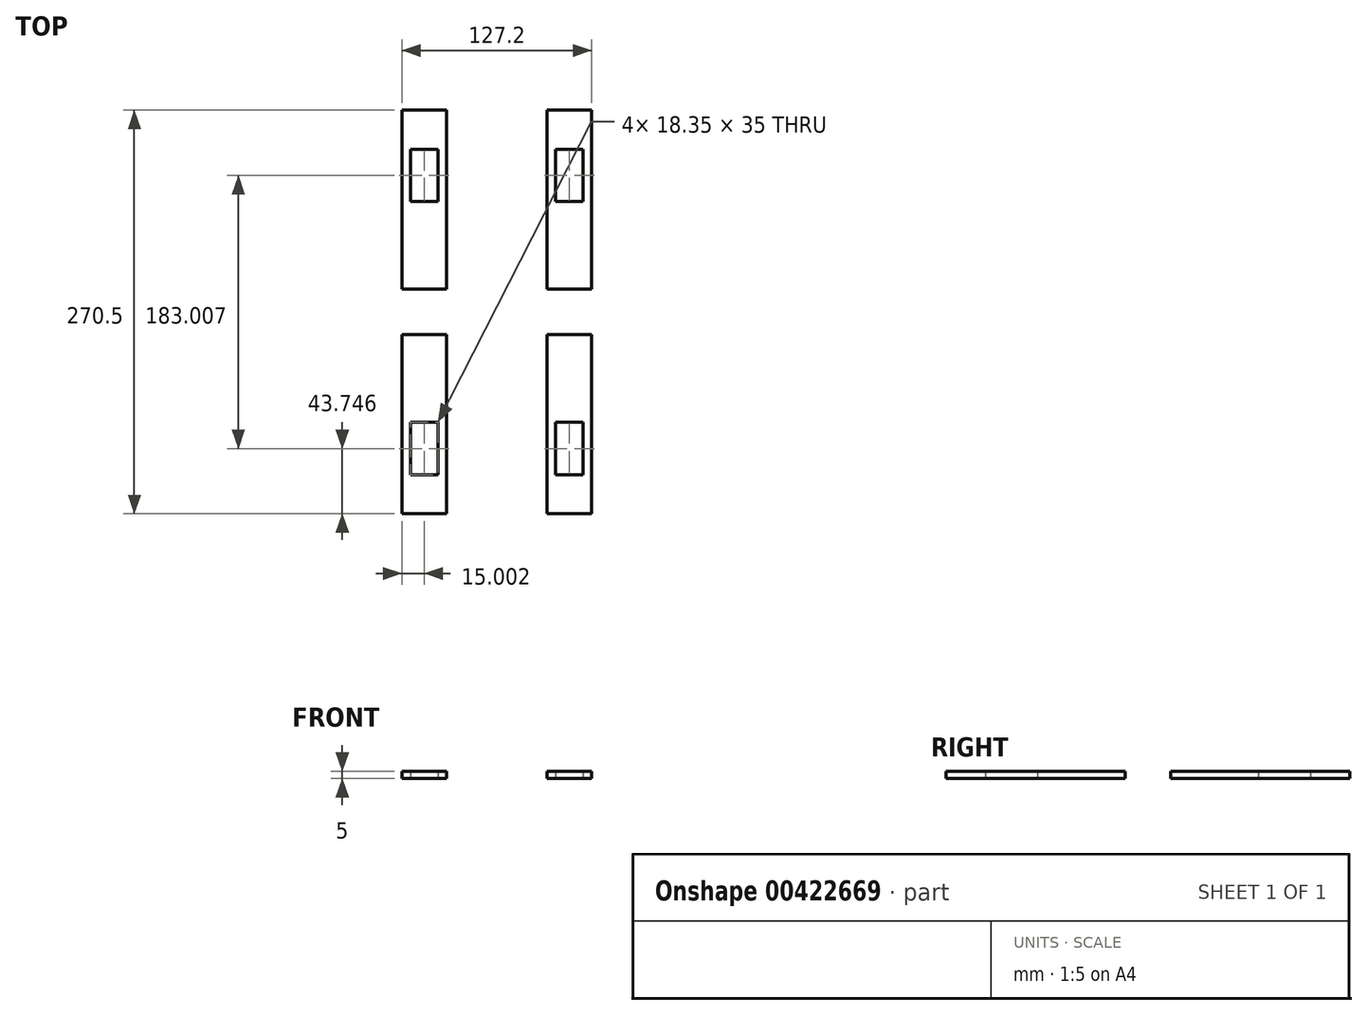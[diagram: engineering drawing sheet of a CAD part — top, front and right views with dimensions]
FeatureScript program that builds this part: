
annotation { "Feature Type Name" : "Feature", "Feature Type Description" : "" }
export const myFeature = defineFeature(function(context is Context, id is Id, definition is map)
    precondition{}
    {
        {
            var Q0;
            Q0=qCreatedBy(makeId("Top.planeOp"),FACE);
            var sketch = newSketch(context, id + "F0", { "sketchPlane" : qUnion([Q0])});
            skLineSegment(sketch, "E0", {"start": v(-63.6, 15.25) * mm, "end": v(-63.6, 135.25) * mm});
            skLineSegment(sketch, "E1", {"start": v(-63.6, 135.25) * mm, "end": v(-33.6, 135.25) * mm});
            skLineSegment(sketch, "E2", {"start": v(-63.6, 15.25) * mm, "end": v(-33.6, 15.25) * mm});
            skLineSegment(sketch, "E3", {"start": v(-33.6, 15.25) * mm, "end": v(-33.6, 135.25) * mm});
            skLineSegment(sketch, "E4.bottom", {"start": v(-39.42, 74) * mm, "end": v(-57.77, 74) * mm});
            skLineSegment(sketch, "E4.top", {"start": v(-39.42, 109) * mm, "end": v(-57.77, 109) * mm});
            skLineSegment(sketch, "E4.left", {"start": v(-39.42, 74) * mm, "end": v(-39.42, 109) * mm});
            skLineSegment(sketch, "E4.right", {"start": v(-57.77, 74) * mm, "end": v(-57.77, 109) * mm});
            skPoint(sketch, "E4.middle", {"position": v(-48.6, 91.5) * mm});
            skLineSegment(sketch, "E5.MirrorCS", {"start": v(-57.77, 74) * mm, "end": v(-39.42, 74) * mm});
            skLineSegment(sketch, "E6.MirrorCS", {"start": v(-57.77, 109) * mm, "end": v(-39.42, 109) * mm});
            skLineSegment(sketch, "E7.MirrorCS", {"start": v(-33.6, 135.25) * mm, "end": v(-63.6, 135.25) * mm});
            skLineSegment(sketch, "E8.MirrorCS", {"start": v(-33.6, 15.25) * mm, "end": v(-63.6, 15.25) * mm});
            skLineSegment(sketch, "E9.MirrorCS", {"start": v(57.77, 74) * mm, "end": v(57.77, 109) * mm});
            skLineSegment(sketch, "E10.MirrorCS", {"start": v(57.77, 74) * mm, "end": v(39.42, 74) * mm});
            skPoint(sketch, "E11.MirrorP", {"position": v(48.6, 91.5) * mm});
            skLineSegment(sketch, "E12.MirrorCS", {"start": v(33.6, 15.25) * mm, "end": v(63.6, 15.25) * mm});
            skLineSegment(sketch, "E13.MirrorCS", {"start": v(39.42, 74) * mm, "end": v(39.42, 109) * mm});
            skLineSegment(sketch, "E14.MirrorCS", {"start": v(57.77, 109) * mm, "end": v(39.42, 109) * mm});
            skLineSegment(sketch, "E15.MirrorCS", {"start": v(39.42, 74) * mm, "end": v(57.77, 74) * mm});
            skLineSegment(sketch, "E16.MirrorCS", {"start": v(63.6, 135.25) * mm, "end": v(33.6, 135.25) * mm});
            skLineSegment(sketch, "E17.MirrorCS", {"start": v(63.6, 15.25) * mm, "end": v(63.6, 135.25) * mm});
            skLineSegment(sketch, "E18.MirrorCS", {"start": v(33.6, 15.25) * mm, "end": v(33.6, 135.25) * mm});
            skLineSegment(sketch, "E19.MirrorCS", {"start": v(33.6, 135.25) * mm, "end": v(63.6, 135.25) * mm});
            skLineSegment(sketch, "E20.MirrorCS", {"start": v(39.42, 109) * mm, "end": v(57.77, 109) * mm});
            skLineSegment(sketch, "E21.MirrorCS", {"start": v(63.6, 15.25) * mm, "end": v(33.6, 15.25) * mm});
            skLineSegment(sketch, "E22.MirrorCS", {"start": v(39.42, -74) * mm, "end": v(57.77, -74) * mm});
            skLineSegment(sketch, "E23.MirrorCS", {"start": v(-39.42, -74) * mm, "end": v(-57.77, -74) * mm});
            skLineSegment(sketch, "E24.MirrorCS", {"start": v(39.42, -109) * mm, "end": v(57.77, -109) * mm});
            skLineSegment(sketch, "E25.MirrorCS", {"start": v(-57.77, -109) * mm, "end": v(-39.42, -109) * mm});
            skLineSegment(sketch, "E26.MirrorCS", {"start": v(-39.42, -109) * mm, "end": v(-57.77, -109) * mm});
            skLineSegment(sketch, "E27.MirrorCS", {"start": v(57.77, -109) * mm, "end": v(39.42, -109) * mm});
            skLineSegment(sketch, "E28.MirrorCS", {"start": v(-57.77, -74) * mm, "end": v(-39.42, -74) * mm});
            skLineSegment(sketch, "E29.MirrorCS", {"start": v(57.77, -74) * mm, "end": v(39.42, -74) * mm});
            skLineSegment(sketch, "E30.MirrorCS", {"start": v(-57.77, -74) * mm, "end": v(-57.77, -109) * mm});
            skLineSegment(sketch, "E31.MirrorCS", {"start": v(39.42, -74) * mm, "end": v(39.42, -109) * mm});
            skLineSegment(sketch, "E32.MirrorCS", {"start": v(57.77, -74) * mm, "end": v(57.77, -109) * mm});
            skLineSegment(sketch, "E33.MirrorCS", {"start": v(-39.42, -74) * mm, "end": v(-39.42, -109) * mm});
            skPoint(sketch, "E34.MirrorP", {"position": v(48.6, -91.5) * mm});
            skPoint(sketch, "E35.MirrorP", {"position": v(-48.6, -91.5) * mm});
            skLineSegment(sketch, "E36.MirrorCS", {"start": v(-63.6, -15.25) * mm, "end": v(-63.6, -135.25) * mm});
            skLineSegment(sketch, "E37.MirrorCS", {"start": v(-33.6, -15.25) * mm, "end": v(-33.6, -135.25) * mm});
            skLineSegment(sketch, "E38.MirrorCS", {"start": v(63.6, -135.25) * mm, "end": v(33.6, -135.25) * mm});
            skLineSegment(sketch, "E39.MirrorCS", {"start": v(33.6, -15.25) * mm, "end": v(33.6, -135.25) * mm});
            skLineSegment(sketch, "E40.MirrorCS", {"start": v(63.6, -15.25) * mm, "end": v(33.6, -15.25) * mm});
            skLineSegment(sketch, "E41.MirrorCS", {"start": v(-33.6, -15.25) * mm, "end": v(-63.6, -15.25) * mm});
            skLineSegment(sketch, "E42.MirrorCS", {"start": v(63.6, -15.25) * mm, "end": v(63.6, -135.25) * mm});
            skLineSegment(sketch, "E43.MirrorCS", {"start": v(-63.6, -135.25) * mm, "end": v(-33.6, -135.25) * mm});
            skLineSegment(sketch, "E44.MirrorCS", {"start": v(33.6, -135.25) * mm, "end": v(63.6, -135.25) * mm});
            skLineSegment(sketch, "E45.MirrorCS", {"start": v(-33.6, -135.25) * mm, "end": v(-63.6, -135.25) * mm});
            skLineSegment(sketch, "E46.MirrorCS", {"start": v(-63.6, -15.25) * mm, "end": v(-33.6, -15.25) * mm});
            skLineSegment(sketch, "E47.MirrorCS", {"start": v(33.6, -15.25) * mm, "end": v(63.6, -15.25) * mm});
            skSolve(sketch);
        }
        {
            var Q0;
            Q0 = qSketchRegion(id + "F0", true);
            extrude(context, id + "F1", {"entities" : qUnion([Q0]), "depth" : 5 * mm});
        }
    });
